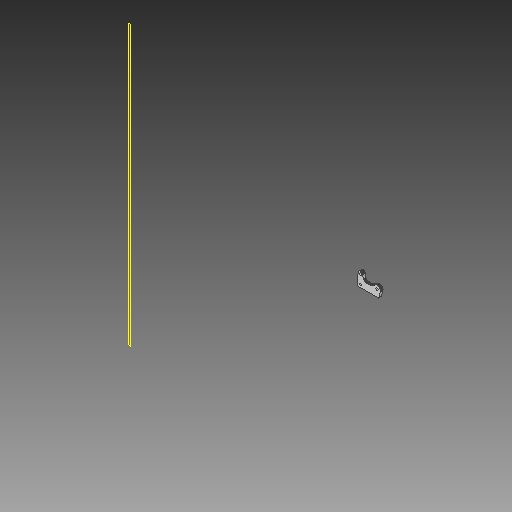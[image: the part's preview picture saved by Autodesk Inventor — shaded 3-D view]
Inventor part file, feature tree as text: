
AUTODESK INVENTOR PART (.ipt)
format: ipt  version: 2018 (Build 220112000, 112)  size: 320,512 bytes
history: native  units: mm
features: other x3, sketch x2, plane x1
ambient origin geometry x8: Origin, YZ Plane, XZ Plane, XY Plane, X Axis, Y Axis, Z Axis, Center Point
bodies: Solid1 (feature_tree)
feature tree (6):
  other  "X-Idler.ipt"
  other  "Solid1::X-Idler.ipt"
  other  "TaggingFeature1"
  sketch  "Sketch1"  dims[d0=10.0mm]
  sketch  "Sketch2"
  plane  "Work Plane1"
